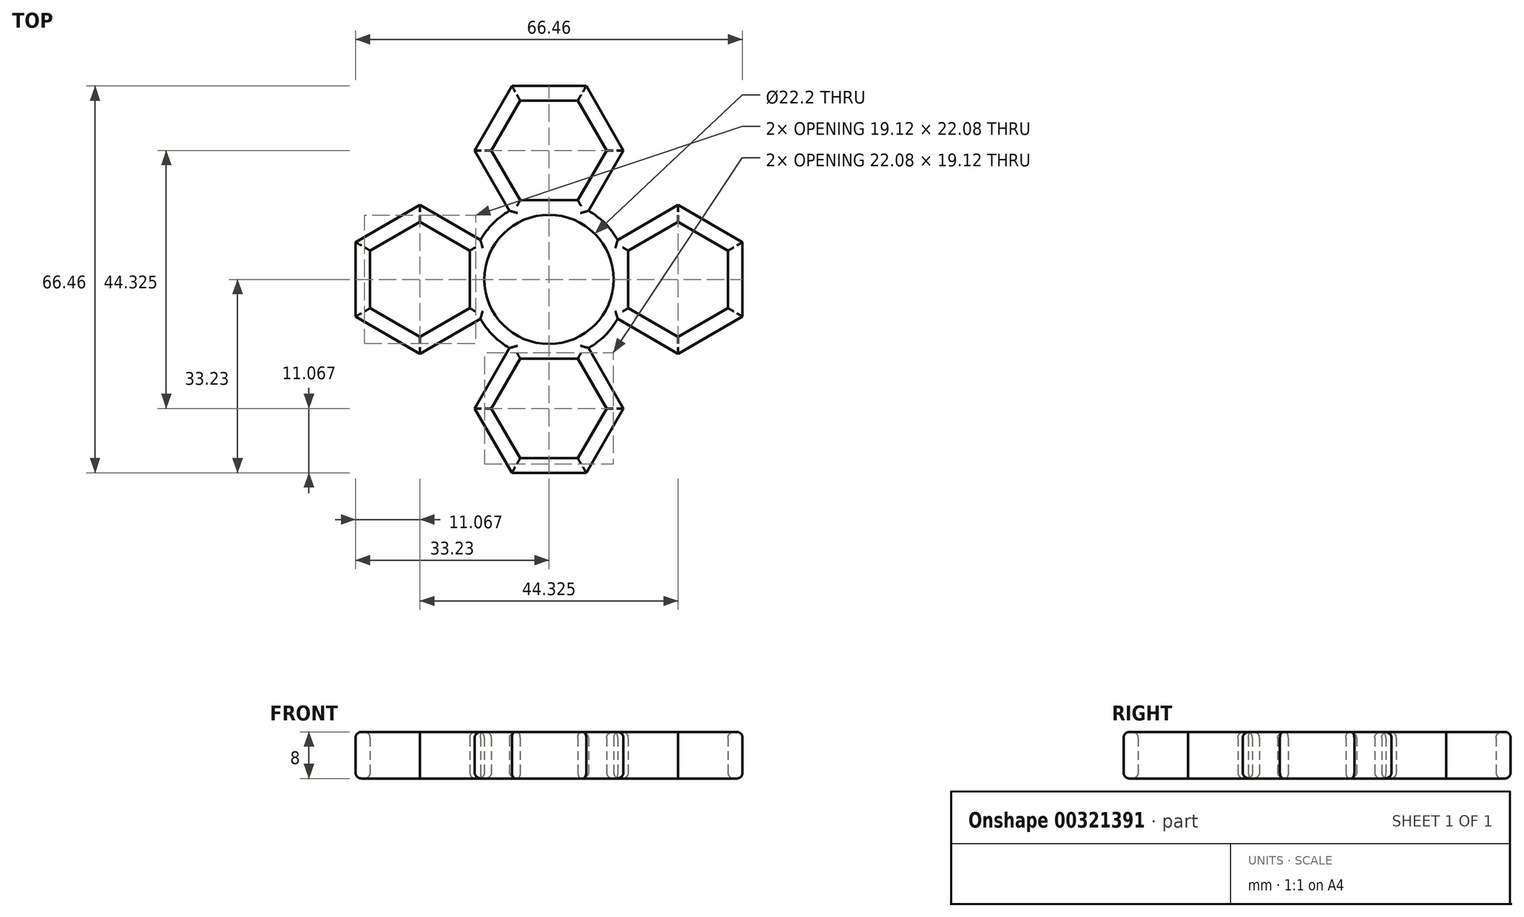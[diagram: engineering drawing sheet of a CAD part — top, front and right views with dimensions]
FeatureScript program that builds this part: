
annotation { "Feature Type Name" : "Feature", "Feature Type Description" : "" }
export const myFeature = defineFeature(function(context is Context, id is Id, definition is map)
    precondition{}
    {
        {
            var Q0;
            Q0=qCreatedBy(makeId("Top.planeOp"),FACE);
            var sketch = newSketch(context, id + "F0", { "sketchPlane" : qUnion([Q0])});
            skCircle(sketch, "E0", {"center": v(0, 0) * mm, "radius": 11.1 * mm});
            skCircle(sketch, "E1", {"center": v(0, 0) * mm, "radius": 13.6 * mm});
            skLineSegment(sketch, "E2", {"start": v(0, 0) * mm, "end": v(0, 13.6) * mm, "construction": true});
            skLineSegment(sketch, "E3", {"start": v(0, 13.6) * mm, "end": v(0, 22.16) * mm, "construction": true});
            skCircle(sketch, "E4.cCircle", {"center": v(0, 22.16) * mm, "radius": 8.56 * mm, "construction": true});
            skLineSegment(sketch, "E4.0", {"start": v(4.94, 13.6) * mm, "end": v(-4.94, 13.6) * mm});
            skLineSegment(sketch, "E4.1", {"start": v(-4.94, 13.6) * mm, "end": v(-9.89, 22.16) * mm});
            skLineSegment(sketch, "E4.2", {"start": v(-9.89, 22.16) * mm, "end": v(-4.94, 30.73) * mm});
            skLineSegment(sketch, "E4.3", {"start": v(-4.94, 30.73) * mm, "end": v(4.94, 30.73) * mm});
            skLineSegment(sketch, "E4.4", {"start": v(4.94, 30.73) * mm, "end": v(9.89, 22.16) * mm});
            skLineSegment(sketch, "E4.5", {"start": v(9.89, 22.16) * mm, "end": v(4.94, 13.6) * mm});
            skPoint(sketch, "E4.0.midPoint", {"position": v(0, 13.6) * mm});
            skCircle(sketch, "E5.cCircle", {"center": v(0, 22.16) * mm, "radius": 11.06 * mm, "construction": true});
            skLineSegment(sketch, "E5.0", {"start": v(6.39, 11.1) * mm, "end": v(-6.39, 11.1) * mm});
            skLineSegment(sketch, "E5.1", {"start": v(-6.39, 11.1) * mm, "end": v(-12.77, 22.16) * mm});
            skLineSegment(sketch, "E5.2", {"start": v(-12.77, 22.16) * mm, "end": v(-6.39, 33.23) * mm});
            skLineSegment(sketch, "E5.3", {"start": v(-6.39, 33.23) * mm, "end": v(6.39, 33.23) * mm});
            skLineSegment(sketch, "E5.4", {"start": v(6.39, 33.23) * mm, "end": v(12.77, 22.16) * mm});
            skLineSegment(sketch, "E5.5", {"start": v(12.77, 22.16) * mm, "end": v(6.39, 11.1) * mm});
            skPoint(sketch, "E5.0.midPoint", {"position": v(0, 11.1) * mm});
            skLineSegment(sketch, "E6.1.0", {"start": v(-33.23, -6.39) * mm, "end": v(-33.23, 6.39) * mm});
            skLineSegment(sketch, "E6.1.1", {"start": v(-33.23, 6.39) * mm, "end": v(-22.16, 12.77) * mm});
            skLineSegment(sketch, "E6.1.2", {"start": v(-22.16, -12.77) * mm, "end": v(-33.23, -6.39) * mm});
            skLineSegment(sketch, "E6.1.3", {"start": v(-11.1, -6.39) * mm, "end": v(-22.16, -12.77) * mm});
            skLineSegment(sketch, "E6.1.4", {"start": v(-11.1, 6.39) * mm, "end": v(-11.1, -6.39) * mm});
            skLineSegment(sketch, "E6.1.5", {"start": v(-22.16, 12.77) * mm, "end": v(-11.1, 6.39) * mm});
            skLineSegment(sketch, "E6.1.6", {"start": v(-22.16, 9.89) * mm, "end": v(-13.6, 4.94) * mm});
            skLineSegment(sketch, "E6.1.7", {"start": v(-13.6, 4.94) * mm, "end": v(-13.6, -4.94) * mm});
            skLineSegment(sketch, "E6.1.8", {"start": v(-13.6, -4.94) * mm, "end": v(-22.16, -9.89) * mm});
            skLineSegment(sketch, "E6.1.9", {"start": v(-22.16, -9.89) * mm, "end": v(-30.73, -4.94) * mm});
            skLineSegment(sketch, "E6.1.10", {"start": v(-30.72, -4.94) * mm, "end": v(-30.73, 4.94) * mm});
            skLineSegment(sketch, "E6.1.11", {"start": v(-30.73, 4.94) * mm, "end": v(-22.16, 9.89) * mm});
            skLineSegment(sketch, "E6.2.0", {"start": v(6.39, -33.23) * mm, "end": v(-6.39, -33.23) * mm});
            skLineSegment(sketch, "E6.2.1", {"start": v(-6.39, -33.23) * mm, "end": v(-12.77, -22.16) * mm});
            skLineSegment(sketch, "E6.2.2", {"start": v(12.77, -22.16) * mm, "end": v(6.39, -33.23) * mm});
            skLineSegment(sketch, "E6.2.3", {"start": v(6.39, -11.1) * mm, "end": v(12.77, -22.16) * mm});
            skLineSegment(sketch, "E6.2.4", {"start": v(-6.39, -11.1) * mm, "end": v(6.39, -11.1) * mm});
            skLineSegment(sketch, "E6.2.5", {"start": v(-12.77, -22.16) * mm, "end": v(-6.39, -11.1) * mm});
            skLineSegment(sketch, "E6.2.6", {"start": v(-9.89, -22.16) * mm, "end": v(-4.94, -13.6) * mm});
            skLineSegment(sketch, "E6.2.7", {"start": v(-4.94, -13.6) * mm, "end": v(4.94, -13.6) * mm});
            skLineSegment(sketch, "E6.2.8", {"start": v(4.94, -13.6) * mm, "end": v(9.89, -22.16) * mm});
            skLineSegment(sketch, "E6.2.9", {"start": v(9.89, -22.16) * mm, "end": v(4.94, -30.73) * mm});
            skLineSegment(sketch, "E6.2.10", {"start": v(4.94, -30.73) * mm, "end": v(-4.94, -30.73) * mm});
            skLineSegment(sketch, "E6.2.11", {"start": v(-4.94, -30.73) * mm, "end": v(-9.89, -22.16) * mm});
            skLineSegment(sketch, "E7.1.3.0", {"start": v(33.23, 6.39) * mm, "end": v(33.23, -6.39) * mm});
            skLineSegment(sketch, "E7.3.3.0", {"start": v(33.23, -6.39) * mm, "end": v(22.16, -12.77) * mm});
            skLineSegment(sketch, "E7.6.3.0", {"start": v(22.16, 12.77) * mm, "end": v(33.23, 6.39) * mm});
            skLineSegment(sketch, "E7.9.3.0", {"start": v(11.1, 6.39) * mm, "end": v(22.16, 12.77) * mm});
            skLineSegment(sketch, "E7.12.3.0", {"start": v(11.1, -6.39) * mm, "end": v(11.1, 6.39) * mm});
            skLineSegment(sketch, "E7.15.3.0", {"start": v(22.16, -12.77) * mm, "end": v(11.1, -6.39) * mm});
            skLineSegment(sketch, "E7.18.3.0", {"start": v(22.16, -9.89) * mm, "end": v(13.6, -4.94) * mm});
            skLineSegment(sketch, "E7.21.3.0", {"start": v(13.6, -4.94) * mm, "end": v(13.6, 4.94) * mm});
            skLineSegment(sketch, "E7.24.3.0", {"start": v(13.6, 4.94) * mm, "end": v(22.16, 9.89) * mm});
            skLineSegment(sketch, "E7.27.3.0", {"start": v(22.16, 9.89) * mm, "end": v(30.73, 4.94) * mm});
            skLineSegment(sketch, "E7.30.3.0", {"start": v(30.73, 4.94) * mm, "end": v(30.73, -4.94) * mm});
            skLineSegment(sketch, "E7.33.3.0", {"start": v(30.73, -4.94) * mm, "end": v(22.16, -9.89) * mm});
            skSolve(sketch);
        }
        {
            var Q0;
            Q0 = qSketchRegion(id + "F0", true);
            extrude(context, id + "F1", {"entities" : qUnion([Q0]), "depth" : 8 * mm, "offsetDistance" : 25 * mm});
        }
        {
            var Q0;
            Q0=makeQuery(id+"F1.opExtrude","CAP_FACE",FACE,{"disambiguationData":[OSD([sQuery(id+"F0.wireOp",EDGE,"E0"),sQuery(id+"F0.wireOp",EDGE,"E1"),sQuery(id+"F0.wireOp",EDGE,"E4.0"),sQuery(id+"F0.wireOp",EDGE,"E4.1"),sQuery(id+"F0.wireOp",EDGE,"E4.2"),sQuery(id+"F0.wireOp",EDGE,"E4.3"),sQuery(id+"F0.wireOp",EDGE,"E4.4"),sQuery(id+"F0.wireOp",EDGE,"E4.5"),sQuery(id+"F0.wireOp",EDGE,"E5.1"),sQuery(id+"F0.wireOp",EDGE,"E5.2"),sQuery(id+"F0.wireOp",EDGE,"E5.3"),sQuery(id+"F0.wireOp",EDGE,"E5.4"),sQuery(id+"F0.wireOp",EDGE,"E5.5"),sQuery(id+"F0.wireOp",EDGE,"E6.1.0"),sQuery(id+"F0.wireOp",EDGE,"E6.1.1"),sQuery(id+"F0.wireOp",EDGE,"E6.1.2"),sQuery(id+"F0.wireOp",EDGE,"E6.1.3"),sQuery(id+"F0.wireOp",EDGE,"E6.1.5"),sQuery(id+"F0.wireOp",EDGE,"E6.1.6"),sQuery(id+"F0.wireOp",EDGE,"E6.1.7"),sQuery(id+"F0.wireOp",EDGE,"E6.1.8"),sQuery(id+"F0.wireOp",EDGE,"E6.1.9"),sQuery(id+"F0.wireOp",EDGE,"E6.1.10"),sQuery(id+"F0.wireOp",EDGE,"E6.1.11"),sQuery(id+"F0.wireOp",EDGE,"E6.2.0"),sQuery(id+"F0.wireOp",EDGE,"E6.2.1"),sQuery(id+"F0.wireOp",EDGE,"E6.2.2"),sQuery(id+"F0.wireOp",EDGE,"E6.2.3"),sQuery(id+"F0.wireOp",EDGE,"E6.2.5"),sQuery(id+"F0.wireOp",EDGE,"E6.2.6"),sQuery(id+"F0.wireOp",EDGE,"E6.2.7"),sQuery(id+"F0.wireOp",EDGE,"E6.2.8"),sQuery(id+"F0.wireOp",EDGE,"E6.2.9"),sQuery(id+"F0.wireOp",EDGE,"E6.2.10"),sQuery(id+"F0.wireOp",EDGE,"E6.2.11"),sQuery(id+"F0.wireOp",EDGE,"E7.1.3.0"),sQuery(id+"F0.wireOp",EDGE,"E7.3.3.0"),sQuery(id+"F0.wireOp",EDGE,"E7.6.3.0"),sQuery(id+"F0.wireOp",EDGE,"E7.9.3.0"),sQuery(id+"F0.wireOp",EDGE,"E7.15.3.0"),sQuery(id+"F0.wireOp",EDGE,"E7.18.3.0"),sQuery(id+"F0.wireOp",EDGE,"E7.21.3.0"),sQuery(id+"F0.wireOp",EDGE,"E7.24.3.0"),sQuery(id+"F0.wireOp",EDGE,"E7.27.3.0"),sQuery(id+"F0.wireOp",EDGE,"E7.30.3.0"),sQuery(id+"F0.wireOp",EDGE,"E7.33.3.0")])],"isStart":false});
            var Q1;
            Q1=makeQuery(id+"F1.opExtrude","CAP_FACE",FACE,{"disambiguationData":[OSD([sQuery(id+"F0.wireOp",EDGE,"E0"),sQuery(id+"F0.wireOp",EDGE,"E1"),sQuery(id+"F0.wireOp",EDGE,"E4.0"),sQuery(id+"F0.wireOp",EDGE,"E4.1"),sQuery(id+"F0.wireOp",EDGE,"E4.2"),sQuery(id+"F0.wireOp",EDGE,"E4.3"),sQuery(id+"F0.wireOp",EDGE,"E4.4"),sQuery(id+"F0.wireOp",EDGE,"E4.5"),sQuery(id+"F0.wireOp",EDGE,"E5.1"),sQuery(id+"F0.wireOp",EDGE,"E5.2"),sQuery(id+"F0.wireOp",EDGE,"E5.3"),sQuery(id+"F0.wireOp",EDGE,"E5.4"),sQuery(id+"F0.wireOp",EDGE,"E5.5"),sQuery(id+"F0.wireOp",EDGE,"E6.1.0"),sQuery(id+"F0.wireOp",EDGE,"E6.1.1"),sQuery(id+"F0.wireOp",EDGE,"E6.1.2"),sQuery(id+"F0.wireOp",EDGE,"E6.1.3"),sQuery(id+"F0.wireOp",EDGE,"E6.1.5"),sQuery(id+"F0.wireOp",EDGE,"E6.1.6"),sQuery(id+"F0.wireOp",EDGE,"E6.1.7"),sQuery(id+"F0.wireOp",EDGE,"E6.1.8"),sQuery(id+"F0.wireOp",EDGE,"E6.1.9"),sQuery(id+"F0.wireOp",EDGE,"E6.1.10"),sQuery(id+"F0.wireOp",EDGE,"E6.1.11"),sQuery(id+"F0.wireOp",EDGE,"E6.2.0"),sQuery(id+"F0.wireOp",EDGE,"E6.2.1"),sQuery(id+"F0.wireOp",EDGE,"E6.2.2"),sQuery(id+"F0.wireOp",EDGE,"E6.2.3"),sQuery(id+"F0.wireOp",EDGE,"E6.2.5"),sQuery(id+"F0.wireOp",EDGE,"E6.2.6"),sQuery(id+"F0.wireOp",EDGE,"E6.2.7"),sQuery(id+"F0.wireOp",EDGE,"E6.2.8"),sQuery(id+"F0.wireOp",EDGE,"E6.2.9"),sQuery(id+"F0.wireOp",EDGE,"E6.2.10"),sQuery(id+"F0.wireOp",EDGE,"E6.2.11"),sQuery(id+"F0.wireOp",EDGE,"E7.1.3.0"),sQuery(id+"F0.wireOp",EDGE,"E7.3.3.0"),sQuery(id+"F0.wireOp",EDGE,"E7.6.3.0"),sQuery(id+"F0.wireOp",EDGE,"E7.9.3.0"),sQuery(id+"F0.wireOp",EDGE,"E7.15.3.0"),sQuery(id+"F0.wireOp",EDGE,"E7.18.3.0"),sQuery(id+"F0.wireOp",EDGE,"E7.21.3.0"),sQuery(id+"F0.wireOp",EDGE,"E7.24.3.0"),sQuery(id+"F0.wireOp",EDGE,"E7.27.3.0"),sQuery(id+"F0.wireOp",EDGE,"E7.30.3.0"),sQuery(id+"F0.wireOp",EDGE,"E7.33.3.0")])],"isStart":true});
            fillet(context, id + "F2", {"entities" : qUnion([Q0, Q1]), "radius" : 1 * mm, "tangentPropagation" : true, "allowEdgeOverflow" : false});
        }
    });
